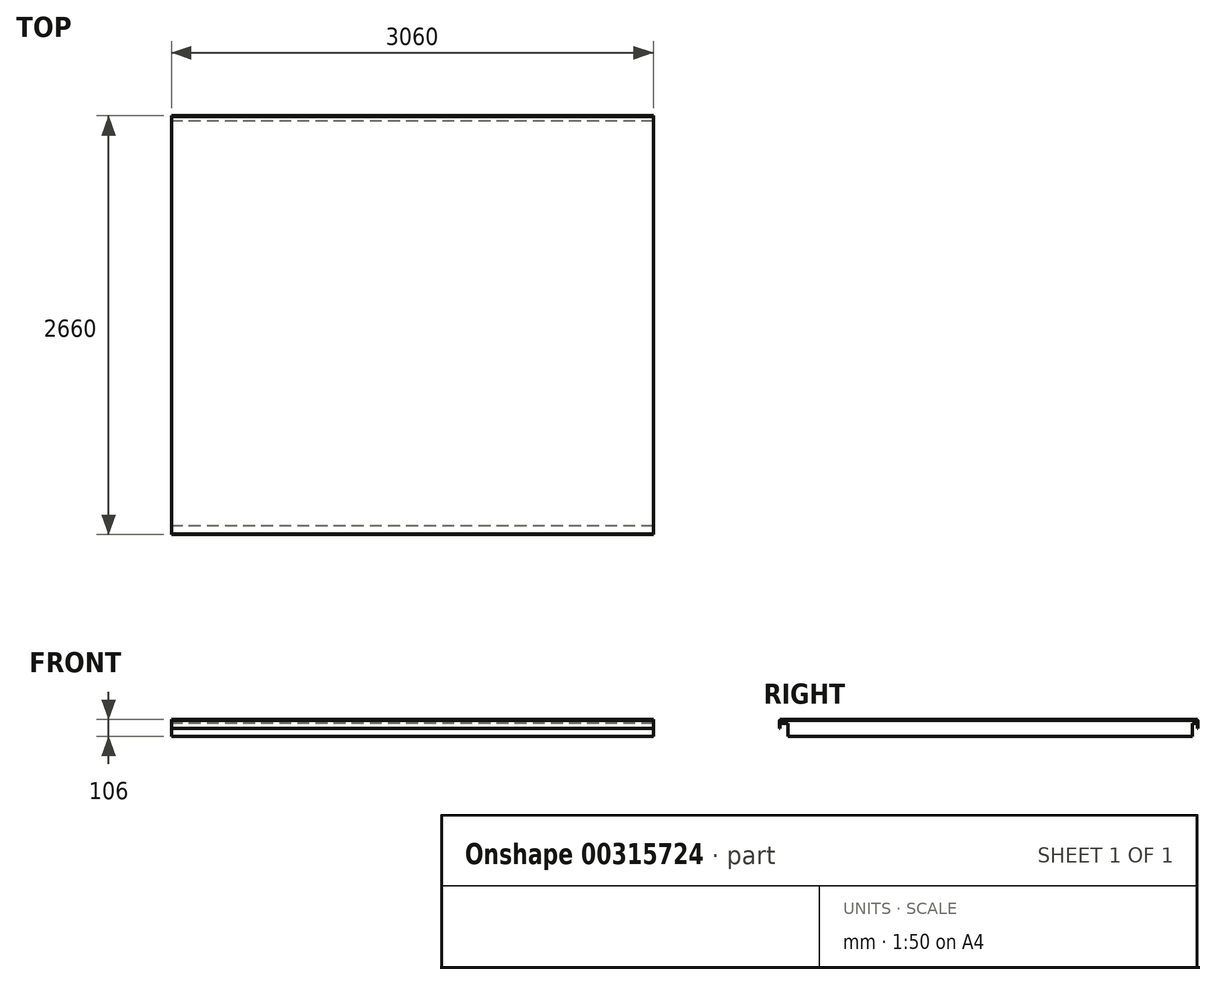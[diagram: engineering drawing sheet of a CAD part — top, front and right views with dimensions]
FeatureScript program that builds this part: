
annotation { "Feature Type Name" : "Feature", "Feature Type Description" : "" }
export const myFeature = defineFeature(function(context is Context, id is Id, definition is map)
    precondition{}
    {
        {
            var Q0;
            Q0=qCreatedBy(makeId("Top.planeOp"),FACE);
            var sketch = newSketch(context, id + "F0", { "sketchPlane" : qUnion([Q0])});
            skLineSegment(sketch, "E0.bottom", {"start": v(0, 0) * mm, "end": v(3060, 0) * mm});
            skLineSegment(sketch, "E0.top", {"start": v(0, 2650) * mm, "end": v(3060, 2650) * mm});
            skLineSegment(sketch, "E0.left", {"start": v(0, 0) * mm, "end": v(0, 2650) * mm});
            skLineSegment(sketch, "E0.right", {"start": v(3060, 0) * mm, "end": v(3060, 2650) * mm});
            skLineSegment(sketch, "E1", {"start": v(0, 2770) * mm, "end": v(3410, 2770) * mm, "construction": true});
            skLineSegment(sketch, "E2", {"start": v(3410, 2770) * mm, "end": v(3410, 0) * mm, "construction": true});
            skSolve(sketch);
        }
        {
            var Q0;
            Q0=qSketchRegion(id+"F0",true);
            extrude(context, id + "F1", {"entities" : qUnion([Q0]), "depth" : 100 * mm});
        }
        {
            var Q0;
            Q0=makeQuery(id+"F1.opExtrude","SWEPT_FACE",FACE,{"disambiguationData":[OSD([sQuery(id+"F0.wireOp",EDGE,"E0.left")])]});
            var sketch = newSketch(context, id + "F2", { "sketchPlane" : qUnion([Q0])});
            skLineSegment(sketch, "E3.bottom", {"start": v(0, 0) * mm, "end": v(-50, 0) * mm});
            skLineSegment(sketch, "E3.top", {"start": v(0, 80) * mm, "end": v(-50, 80) * mm});
            skLineSegment(sketch, "E3.left", {"start": v(0, 0) * mm, "end": v(0, 80) * mm});
            skLineSegment(sketch, "E3.right", {"start": v(-50, 0) * mm, "end": v(-50, 80) * mm});
            skLineSegment(sketch, "E4.bottom", {"start": v(-2650, 0) * mm, "end": v(-2620, 0) * mm});
            skLineSegment(sketch, "E4.top", {"start": v(-2650, 80) * mm, "end": v(-2620, 80) * mm});
            skLineSegment(sketch, "E4.left", {"start": v(-2650, 0) * mm, "end": v(-2650, 80) * mm});
            skLineSegment(sketch, "E4.right", {"start": v(-2620, 0) * mm, "end": v(-2620, 80) * mm});
            skSolve(sketch);
        }
        {
            var Q0;
            Q0=qSketchRegion(id+"F2",true);
            extrude(context, id + "F3", {"entities" : qUnion([Q0]), "operationType" : NewBodyOperationType.REMOVE, "endBound" : BoundingType.THROUGH_ALL, "oppositeDirection" : true, "depth" : 25 * mm});
        }
        {
            var Q0;
            Q0=makeQuery(id+"F1.opExtrude","CAP_FACE",FACE,{"disambiguationData":[OSD([sQuery(id+"F0.wireOp",EDGE,"E0.bottom"),sQuery(id+"F0.wireOp",EDGE,"E0.top"),sQuery(id+"F0.wireOp",EDGE,"E0.left"),sQuery(id+"F0.wireOp",EDGE,"E0.right")])],"isStart":false});
            var sketch = newSketch(context, id + "F4", { "sketchPlane" : qUnion([Q0])});
            skLineSegment(sketch, "E5.bottom", {"start": v(0, 0) * mm, "end": v(3060, 0) * mm});
            skLineSegment(sketch, "E5.top", {"start": v(0, 2650) * mm, "end": v(3060, 2650) * mm});
            skLineSegment(sketch, "E5.left", {"start": v(0, 0) * mm, "end": v(0, 2650) * mm});
            skLineSegment(sketch, "E5.right", {"start": v(3060, 0) * mm, "end": v(3060, 2650) * mm});
            skSolve(sketch);
        }
        {
            var Q0;
            Q0=qSketchRegion(id+"F4",true);
            extrude(context, id + "F5", {"entities" : qUnion([Q0]), "depth" : 6 * mm});
        }
        {
            var Q0;
            Q0=makeQuery(id+"F1.opExtrude","SWEPT_FACE",FACE,{"disambiguationData":[OSD([sQuery(id+"F0.wireOp",EDGE,"E0.bottom")])]});
            var sketch = newSketch(context, id + "F6", { "sketchPlane" : qUnion([Q0])});
            skLineSegment(sketch, "E6.bottom", {"start": v(0, 100) * mm, "end": v(3060, 100) * mm});
            skLineSegment(sketch, "E6.top", {"start": v(0, 50) * mm, "end": v(3060, 50) * mm});
            skLineSegment(sketch, "E6.left", {"start": v(0, 100) * mm, "end": v(0, 50) * mm});
            skLineSegment(sketch, "E6.right", {"start": v(3060, 100) * mm, "end": v(3060, 50) * mm});
            skSolve(sketch);
        }
        {
            var Q0;
            Q0=qSketchRegion(id+"F6",true);
            extrude(context, id + "F7", {"entities" : qUnion([Q0]), "depth" : 5 * mm});
        }
        {
            var Q0;
            Q0=makeQuery(id+"F1.opExtrude","SWEPT_FACE",FACE,{"disambiguationData":[OSD([sQuery(id+"F0.wireOp",EDGE,"E0.top")])]});
            var sketch = newSketch(context, id + "F8", { "sketchPlane" : qUnion([Q0])});
            skLineSegment(sketch, "E7.bottom", {"start": v(-3060, 100) * mm, "end": v(0, 100) * mm});
            skLineSegment(sketch, "E7.top", {"start": v(-3060, 50) * mm, "end": v(0, 50) * mm});
            skLineSegment(sketch, "E7.left", {"start": v(-3060, 100) * mm, "end": v(-3060, 50) * mm});
            skLineSegment(sketch, "E7.right", {"start": v(0, 100) * mm, "end": v(0, 50) * mm});
            skSolve(sketch);
        }
        {
            var Q0;
            Q0=qSketchRegion(id+"F8",true);
            extrude(context, id + "F9", {"entities" : qUnion([Q0]), "depth" : 5 * mm});
        }
    });
